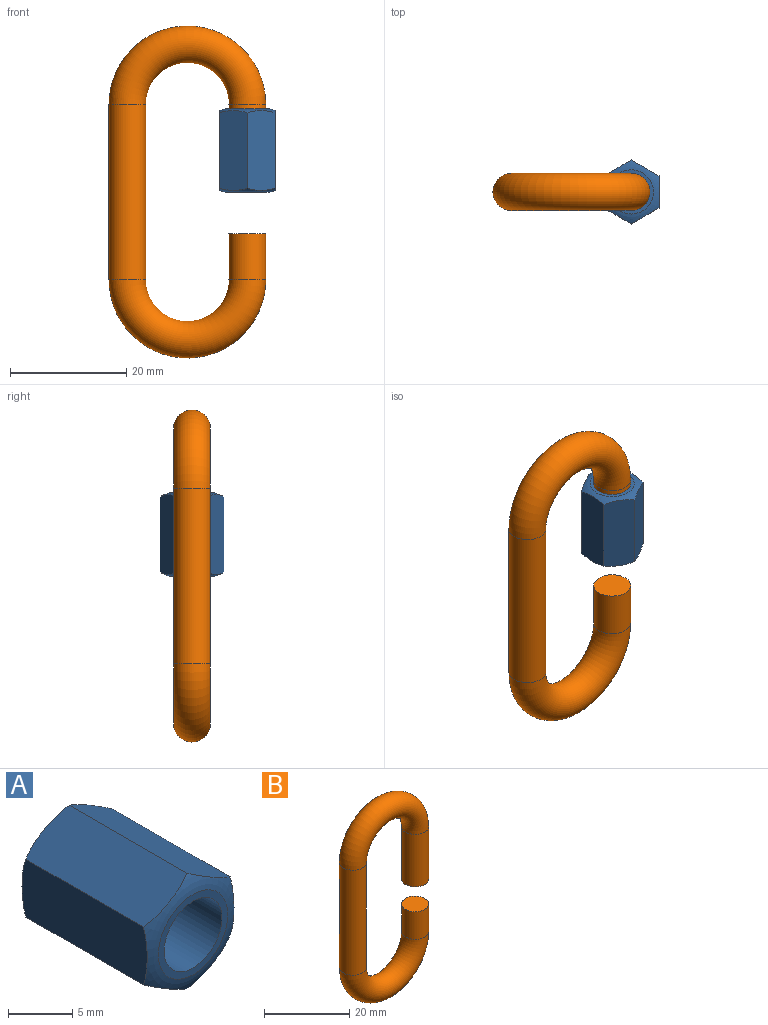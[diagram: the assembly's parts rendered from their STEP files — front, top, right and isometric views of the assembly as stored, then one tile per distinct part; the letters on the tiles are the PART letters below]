
ASSEMBLY  parts=2 mates=1
PART A: 11 faces, bbox 11x14.3x11 mm
  f0: plane 7.63x7.63mm, normal (0,-1,0), area 14mm2, adj f1,f3
  f1: cylinder r=3.17mm len=14.29mm, axis (0,1,0), area 285mm2, adj f0,f2
  f2: plane 7.62x7.62mm, normal (0,1,0), area 13.8mm2, adj f1,f10
  f3: torus R=3.28mm, axis (0,1,0), area 34.9mm2, adj f0,f4,f5,f6,f7,f8,f9
  f4: plane 13.75x5.5mm, normal (-1,0,0), area 74.2mm2, adj f3,f5,f9,f10
  f5: plane 13.75x4.77mm, normal (-0.5,0,0.87), area 74.2mm2, adj f3,f4,f6,f10
  f6: plane 13.75x4.77mm, normal (0.5,0,0.87), area 74.2mm2, adj f3,f5,f7,f10
  f7: plane 13.75x5.5mm, normal (1,0,0), area 74.2mm2, adj f3,f6,f8,f10
  f8: plane 13.75x4.77mm, normal (0.5,0,-0.87), area 74.2mm2, adj f3,f7,f9,f10
  f9: plane 13.75x4.77mm, normal (-0.5,0,-0.87), area 74.2mm2, adj f3,f4,f8,f10
  f10: torus R=3.28mm, axis (0,1,0), area 35.1mm2, adj f2,f4,f5,f6,f7,f8,f9
PART B: 7 faces, bbox 29.2x6.4x59.4 mm
  f0: plane 6.35x6.35mm, normal (0,0,1), area 31.7mm2, adj f6
  f1: plane 6.35x6.35mm, normal (0,0,-1), area 31.7mm2, adj f2
  f2: cylinder r=3.17mm len=15.08mm, axis (0,0,1), area 300.9mm2, adj f1,f3
  f3: torus R=10.32mm, axis (0,-1,0), area 646.7mm2, adj f2,f4
  f4: cylinder r=3.17mm len=30.16mm, axis (0,0,-1), area 601.7mm2, adj f3,f5
  f5: torus R=10.32mm, axis (0,-1,0), area 646.7mm2, adj f4,f6
  f6: cylinder r=3.17mm len=7.94mm, axis (0,0,1), area 158.3mm2, adj f0,f5
PLACE A rot(axis=(1,0,0),90deg) t=(-7.53,-4.61,15.81)mm
PLACE B t=(-17.85,-4.61,8.66)mm
MATE fastened A.f1 <-> B.f2  axis (0,0,1) through (-7.53,-4.61,8.66)mm
